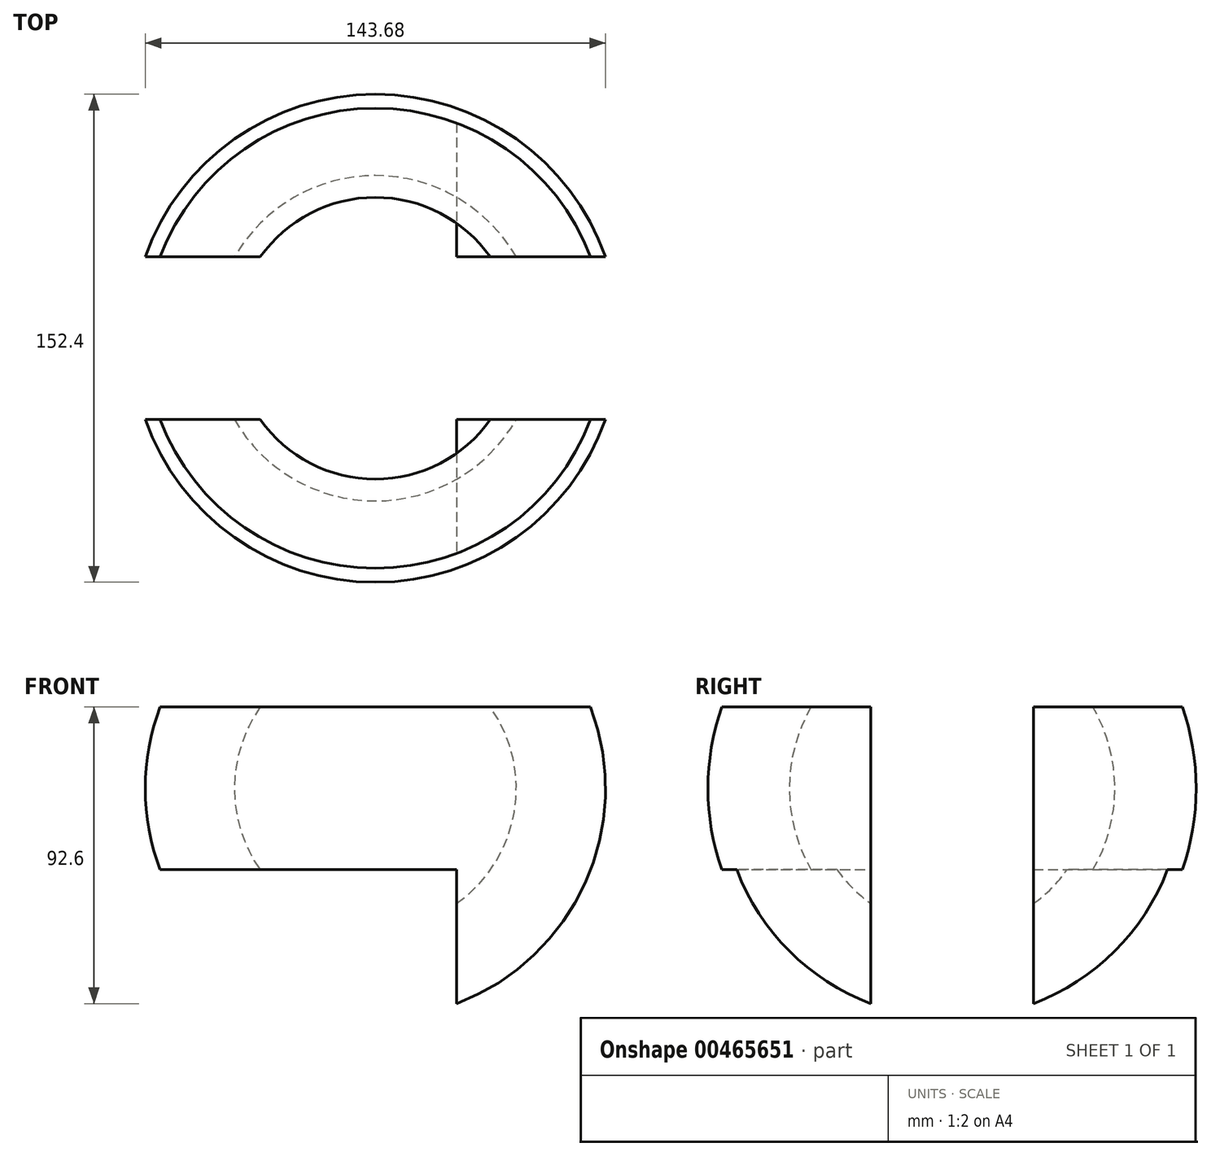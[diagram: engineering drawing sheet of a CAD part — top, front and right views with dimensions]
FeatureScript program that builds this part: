
annotation { "Feature Type Name" : "Feature", "Feature Type Description" : "" }
export const myFeature = defineFeature(function(context is Context, id is Id, definition is map)
    precondition{}
    {
        {
            var Q0;
            Q0=qCreatedBy(makeId("Front.planeOp"),FACE);
            var sketch = newSketch(context, id + "F0", { "sketchPlane" : qUnion([Q0])});
            skArc(sketch, "E0", {"start": v(0, -76.2) * mm, "mid": v(76.2, 0) * mm, "end": v(0, 76.2) * mm});
            skLineSegment(sketch, "E1", {"start": v(0, 0) * mm, "end": v(0, 76.2) * mm});
            skLineSegment(sketch, "E2", {"start": v(0, 76.2) * mm, "end": v(0, -76.2) * mm});
            skSolve(sketch);
        }
        {
            var Q0;
            {var subQ0=sQuery(id+"F0.wireOp",EDGE,"E0");Q0=makeQuery(id+"F0.imprint","IMPRINT",FACE,{"disambiguationData":[TD([[makeQuery(id+"F0.imprint","IMPRINT",EDGE,{"derivedFrom":subQ0}),1.0]])]});}
            var Q1;
            Q1=sQuery(id+"F0.wireOp",EDGE,"E2");
            revolve(context, id + "F1", {"entities" : qUnion([Q0]), "axis" : qUnion([Q1]), "revolveType" : RevolveType.FULL});
        }
        {
            var Q0;
            Q0=qCreatedBy(makeId("Front.planeOp"),FACE);
            var sketch = newSketch(context, id + "F2", { "sketchPlane" : qUnion([Q0])});
            skCircle(sketch, "E3", {"center": v(0, 0) * mm, "radius": 76.2 * mm});
            skLineSegment(sketch, "E4", {"start": v(-25.4, 71.84) * mm, "end": v(-25.4, -71.84) * mm});
            skLineSegment(sketch, "E5", {"start": v(25.4, 71.84) * mm, "end": v(25.4, -71.84) * mm});
            skLineSegment(sketch, "E6", {"start": v(-71.84, 25.4) * mm, "end": v(71.84, 25.4) * mm});
            skLineSegment(sketch, "E7", {"start": v(-71.84, -25.4) * mm, "end": v(71.84, -25.4) * mm});
            skSolve(sketch);
        }
        {
            var Q0;
            Q0=qCreatedBy(makeId("Right.planeOp"),FACE);
            var sketch = newSketch(context, id + "F3", { "sketchPlane" : qUnion([Q0])});
            skCircle(sketch, "E8", {"center": v(0, 0) * mm, "radius": 76.2 * mm});
            skLineSegment(sketch, "E9", {"start": v(-25.4, -71.84) * mm, "end": v(-25.4, 71.84) * mm});
            skLineSegment(sketch, "E10", {"start": v(25.4, -71.84) * mm, "end": v(25.4, 71.84) * mm});
            skLineSegment(sketch, "E11", {"start": v(-71.84, 25.4) * mm, "end": v(71.84, 25.4) * mm});
            skLineSegment(sketch, "E12", {"start": v(-71.84, -25.4) * mm, "end": v(71.84, -25.4) * mm});
            skSolve(sketch);
        }
        {
            var Q0;
            {var subQ0=sQuery(id+"F2.wireOp",EDGE,"E4");var subQ1=sQuery(id+"F2.wireOp",EDGE,"E3");var subQ2=makeQuery(id+"F2.imprint","INTERSECT",VERTEX,{"disambiguationData":[OD(0.0)],"derivedFrom":[subQ1,subQ0]});Q0=makeQuery(id+"F2.imprint","IMPRINT",FACE,{"disambiguationData":[TD([[makeQuery(id+"F2.imprint","IMPRINT",EDGE,{"disambiguationData":[TD([[subQ2,-1.0]])],"derivedFrom":subQ1}),1.0]])]});}
            var Q1;
            {var subQ0=sQuery(id+"F2.wireOp",EDGE,"E6");var subQ1=sQuery(id+"F2.wireOp",EDGE,"E3");var subQ2=makeQuery(id+"F2.imprint","INTERSECT",VERTEX,{"disambiguationData":[OD(0.0)],"derivedFrom":[subQ1,subQ0]});Q1=makeQuery(id+"F2.imprint","IMPRINT",FACE,{"disambiguationData":[TD([[makeQuery(id+"F2.imprint","IMPRINT",EDGE,{"disambiguationData":[TD([[subQ2,-1.0]])],"derivedFrom":subQ1}),1.0]])]});}
            var Q2;
            {var subQ0=sQuery(id+"F2.wireOp",EDGE,"E4");var subQ1=sQuery(id+"F2.wireOp",EDGE,"E3");var subQ2=makeQuery(id+"F2.imprint","INTERSECT",VERTEX,{"disambiguationData":[OD(1.0)],"derivedFrom":[subQ1,subQ0]});Q2=makeQuery(id+"F2.imprint","IMPRINT",FACE,{"disambiguationData":[TD([[makeQuery(id+"F2.imprint","IMPRINT",EDGE,{"disambiguationData":[TD([[subQ2,1.0]])],"derivedFrom":subQ1}),1.0]])]});}
            var Q3;
            {var subQ0=sQuery(id+"F2.wireOp",EDGE,"E4");var subQ1=sQuery(id+"F2.wireOp",EDGE,"E3");var subQ2=makeQuery(id+"F2.imprint","INTERSECT",VERTEX,{"disambiguationData":[OD(1.0)],"derivedFrom":[subQ1,subQ0]});Q3=makeQuery(id+"F2.imprint","IMPRINT",FACE,{"disambiguationData":[TD([[makeQuery(id+"F2.imprint","IMPRINT",EDGE,{"disambiguationData":[TD([[subQ2,-1.0]])],"derivedFrom":subQ1}),1.0]])]});}
            var Q4;
            {var subQ0=sQuery(id+"F2.wireOp",EDGE,"E5");var subQ1=sQuery(id+"F2.wireOp",EDGE,"E3");var subQ2=makeQuery(id+"F2.imprint","INTERSECT",VERTEX,{"disambiguationData":[OD(1.0)],"derivedFrom":[subQ1,subQ0]});Q4=makeQuery(id+"F2.imprint","IMPRINT",FACE,{"disambiguationData":[TD([[makeQuery(id+"F2.imprint","IMPRINT",EDGE,{"disambiguationData":[TD([[subQ2,-1.0]])],"derivedFrom":subQ1}),1.0]])]});}
            var Q5;
            {var subQ0=sQuery(id+"F2.wireOp",EDGE,"E6");var subQ1=sQuery(id+"F2.wireOp",EDGE,"E3");var subQ2=makeQuery(id+"F2.imprint","INTERSECT",VERTEX,{"disambiguationData":[OD(1.0)],"derivedFrom":[subQ1,subQ0]});Q5=makeQuery(id+"F2.imprint","IMPRINT",FACE,{"disambiguationData":[TD([[makeQuery(id+"F2.imprint","IMPRINT",EDGE,{"disambiguationData":[TD([[subQ2,1.0]])],"derivedFrom":subQ1}),1.0]])]});}
            var Q6;
            {var subQ0=sQuery(id+"F2.wireOp",EDGE,"E5");var subQ1=sQuery(id+"F2.wireOp",EDGE,"E3");var subQ2=makeQuery(id+"F2.imprint","INTERSECT",VERTEX,{"disambiguationData":[OD(0.0)],"derivedFrom":[subQ1,subQ0]});Q6=makeQuery(id+"F2.imprint","IMPRINT",FACE,{"disambiguationData":[TD([[makeQuery(id+"F2.imprint","IMPRINT",EDGE,{"disambiguationData":[TD([[subQ2,1.0]])],"derivedFrom":subQ1}),1.0]])]});}
            extrude(context, id + "F4", {"entities" : qUnion([Q0, Q1, Q2, Q3, Q4, Q5, Q6]), "operationType" : NewBodyOperationType.REMOVE, "endBound" : BoundingType.SYMMETRIC, "oppositeDirection" : true, "depth" : 254 * mm, "offsetDistance" : 25.4 * mm});
        }
        {
            var Q0;
            {var subQ0=sQuery(id+"F3.wireOp",EDGE,"E9");var subQ1=sQuery(id+"F3.wireOp",EDGE,"E8");var subQ2=makeQuery(id+"F3.imprint","INTERSECT",VERTEX,{"disambiguationData":[OD(1.0)],"derivedFrom":[subQ1,subQ0]});Q0=makeQuery(id+"F3.imprint","IMPRINT",FACE,{"disambiguationData":[TD([[makeQuery(id+"F3.imprint","IMPRINT",EDGE,{"disambiguationData":[TD([[subQ2,-1.0]])],"derivedFrom":subQ1}),1.0]])]});}
            var Q1;
            {var subQ0=sQuery(id+"F3.wireOp",EDGE,"E11");var subQ1=sQuery(id+"F3.wireOp",EDGE,"E8");var subQ2=makeQuery(id+"F3.imprint","INTERSECT",VERTEX,{"disambiguationData":[OD(0.0)],"derivedFrom":[subQ1,subQ0]});Q1=makeQuery(id+"F3.imprint","IMPRINT",FACE,{"disambiguationData":[TD([[makeQuery(id+"F3.imprint","IMPRINT",EDGE,{"disambiguationData":[TD([[subQ2,-1.0]])],"derivedFrom":subQ1}),1.0]])]});}
            var Q2;
            {var subQ0=sQuery(id+"F3.wireOp",EDGE,"E12");var subQ1=sQuery(id+"F3.wireOp",EDGE,"E9");var subQ2=makeQuery(id+"F3.imprint","INTERSECT",VERTEX,{"derivedFrom":[subQ1,subQ0]});Q2=makeQuery(id+"F3.imprint","IMPRINT",FACE,{"disambiguationData":[TD([[makeQuery(id+"F3.imprint","IMPRINT",EDGE,{"disambiguationData":[TD([[subQ2,-1.0]])],"derivedFrom":subQ1}),-1.0]])]});}
            var Q3;
            {var subQ0=sQuery(id+"F3.wireOp",EDGE,"E11");var subQ1=sQuery(id+"F3.wireOp",EDGE,"E8");var subQ2=makeQuery(id+"F3.imprint","INTERSECT",VERTEX,{"disambiguationData":[OD(1.0)],"derivedFrom":[subQ1,subQ0]});Q3=makeQuery(id+"F3.imprint","IMPRINT",FACE,{"disambiguationData":[TD([[makeQuery(id+"F3.imprint","IMPRINT",EDGE,{"disambiguationData":[TD([[subQ2,1.0]])],"derivedFrom":subQ1}),1.0]])]});}
            var Q4;
            {var subQ0=sQuery(id+"F3.wireOp",EDGE,"E10");var subQ1=sQuery(id+"F3.wireOp",EDGE,"E8");var subQ2=makeQuery(id+"F3.imprint","INTERSECT",VERTEX,{"disambiguationData":[OD(1.0)],"derivedFrom":[subQ1,subQ0]});Q4=makeQuery(id+"F3.imprint","IMPRINT",FACE,{"disambiguationData":[TD([[makeQuery(id+"F3.imprint","IMPRINT",EDGE,{"disambiguationData":[TD([[subQ2,1.0]])],"derivedFrom":subQ1}),1.0]])]});}
            extrude(context, id + "F5", {"entities" : qUnion([Q0, Q1, Q2, Q3, Q4]), "operationType" : NewBodyOperationType.REMOVE, "endBound" : BoundingType.SYMMETRIC, "depth" : 254 * mm, "offsetDistance" : 25.4 * mm});
        }
        {
            var Q0;
            Q0=qCreatedBy(makeId("Front.planeOp"),FACE);
            var sketch = newSketch(context, id + "F6", { "sketchPlane" : qUnion([Q0])});
            skCircle(sketch, "E13", {"center": v(0, 0) * mm, "radius": 50.8 * mm});
            skLineSegment(sketch, "E14", {"start": v(0, 0) * mm, "end": v(-50.8, 0) * mm});
            skLineSegment(sketch, "E15", {"start": v(0, 0) * mm, "end": v(50.8, 0) * mm});
            skCircle(sketch, "E16", {"center": v(0, 0) * mm, "radius": 73.66 * mm});
            skCircle(sketch, "E17", {"center": v(0, 0) * mm, "radius": 79.16 * mm});
            skLineSegment(sketch, "E18", {"start": v(50.8, 0) * mm, "end": v(79.16, 0) * mm});
            skLineSegment(sketch, "E19", {"start": v(-50.8, 0) * mm, "end": v(-79.16, 0) * mm});
            skSolve(sketch);
        }
        {
            var Q0;
            {var subQ0=sQuery(id+"F6.wireOp",EDGE,"E14");Q0=makeQuery(id+"F6.imprint","IMPRINT",FACE,{"disambiguationData":[TD([[makeQuery(id+"F6.imprint","IMPRINT",EDGE,{"derivedFrom":subQ0}),-1.0]])]});}
            var Q1;
            Q1=sQuery(id+"F6.wireOp",EDGE,"E15");
            revolve(context, id + "F7", {"operationType" : NewBodyOperationType.REMOVE, "surfaceOperationType" : NewSurfaceOperationType.NEW, "entities" : qUnion([Q0]), "axis" : qUnion([Q1]), "revolveType" : RevolveType.FULL, "oppositeDirection" : true});
        }
    });
